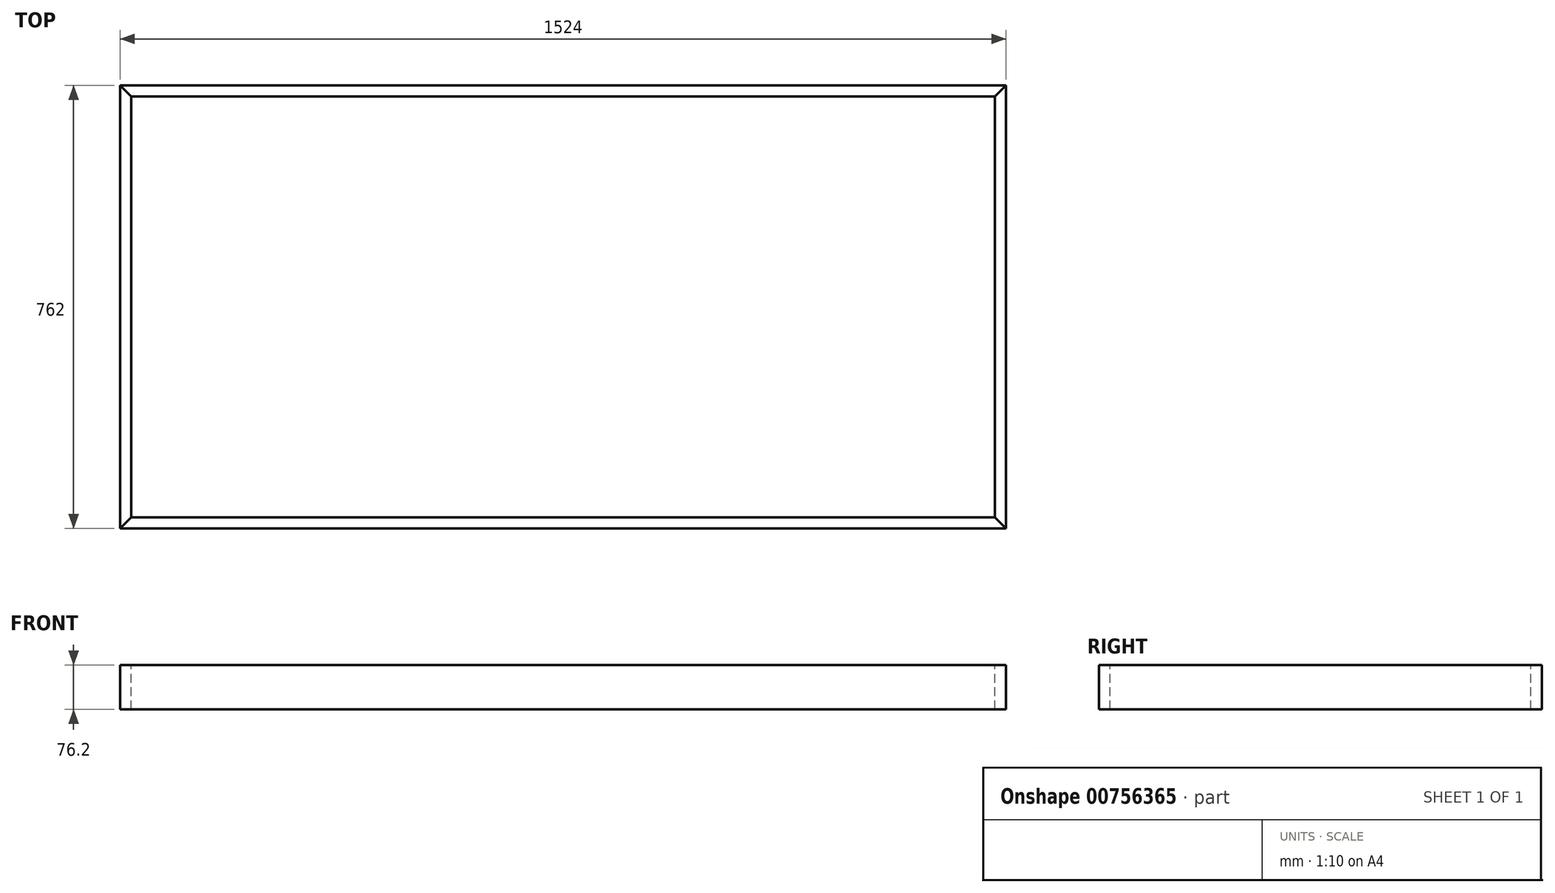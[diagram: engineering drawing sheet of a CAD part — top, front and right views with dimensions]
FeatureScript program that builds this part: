
annotation { "Feature Type Name" : "Feature", "Feature Type Description" : "" }
export const myFeature = defineFeature(function(context is Context, id is Id, definition is map)
    precondition{}
    {
        {
            var Q0;
            Q0=qCreatedBy(makeId("Top.planeOp"),FACE);
            var sketch = newSketch(context, id + "F0", { "sketchPlane" : qUnion([Q0])});
            skLineSegment(sketch, "E0.bottom", {"start": v(762, -381) * mm, "end": v(-762, -381) * mm});
            skLineSegment(sketch, "E0.top", {"start": v(762, 381) * mm, "end": v(-762, 381) * mm});
            skLineSegment(sketch, "E0.left", {"start": v(762, -381) * mm, "end": v(762, 381) * mm});
            skLineSegment(sketch, "E0.right", {"start": v(-762, -381) * mm, "end": v(-762, 381) * mm});
            skPoint(sketch, "E0.middle", {"position": v(0, 0) * mm});
            skSolve(sketch);
        }
        {
            var Q0;
            Q0=qCreatedBy(makeId("Top.planeOp"),FACE);
            var sketch = newSketch(context, id + "F1", { "sketchPlane" : qUnion([Q0])});
            skLineSegment(sketch, "E1.bottom", {"start": v(762, -381) * mm, "end": v(-762, -381) * mm});
            skLineSegment(sketch, "E1.top", {"start": v(762, 381) * mm, "end": v(-762, 381) * mm});
            skLineSegment(sketch, "E1.left", {"start": v(762, -381) * mm, "end": v(762, 381) * mm});
            skLineSegment(sketch, "E1.right", {"start": v(-762, -381) * mm, "end": v(-762, 381) * mm});
            skPoint(sketch, "E1.middle", {"position": v(0, 0) * mm});
            skLineSegment(sketch, "E2.0", {"start": v(742.95, 361.95) * mm, "end": v(-742.95, 361.95) * mm});
            skLineSegment(sketch, "E2.1", {"start": v(742.95, -361.95) * mm, "end": v(742.95, 361.95) * mm});
            skLineSegment(sketch, "E2.2", {"start": v(742.95, -361.95) * mm, "end": v(-742.95, -361.95) * mm});
            skLineSegment(sketch, "E2.3", {"start": v(-742.95, -361.95) * mm, "end": v(-742.95, 361.95) * mm});
            skLineSegment(sketch, "E3", {"start": v(-762, 381) * mm, "end": v(-742.95, 361.95) * mm});
            skLineSegment(sketch, "E4", {"start": v(742.95, 361.95) * mm, "end": v(762, 381) * mm});
            skLineSegment(sketch, "E5", {"start": v(742.95, -361.95) * mm, "end": v(762, -381) * mm});
            skLineSegment(sketch, "E6", {"start": v(-762, -381) * mm, "end": v(-742.95, -361.95) * mm});
            skSolve(sketch);
        }
        {
            var Q0;
            Q0=makeQuery(id+"F1.imprint","IMPRINT",FACE,{"disambiguationData":[TD([[makeQuery(id+"F1.imprint","IMPRINT",EDGE,{"derivedFrom":sQuery(id+"F1.wireOp",EDGE,"E1.right")}),-1.0]])]});
            extrude(context, id + "F2", {"entities" : qUnion([Q0]), "oppositeDirection" : true, "depth" : 76.2 * mm, "offsetDistance" : 25.4 * mm});
        }
        {
            var Q0;
            Q0=makeQuery(id+"F1.imprint","IMPRINT",FACE,{"disambiguationData":[TD([[makeQuery(id+"F1.imprint","IMPRINT",EDGE,{"derivedFrom":sQuery(id+"F1.wireOp",EDGE,"E1.top")}),1.0]])]});
            extrude(context, id + "F3", {"entities" : qUnion([Q0]), "oppositeDirection" : true, "depth" : 76.2 * mm, "offsetDistance" : 25.4 * mm});
        }
        {
            var Q0;
            Q0=makeQuery(id+"F3.opExtrude","SWEPT_BODY",BODY,{"disambiguationData":[OSD([sQuery(id+"F1.wireOp",EDGE,"E1.top"),sQuery(id+"F1.wireOp",EDGE,"E2.0"),sQuery(id+"F1.wireOp",EDGE,"E3"),sQuery(id+"F1.wireOp",EDGE,"E4")])]});
            var Q1;
            Q1=qCreatedBy(makeId("Front.planeOp"),FACE);
            mirror(context, id + "F4", {"entities" : qUnion([Q0]), "mirrorPlane" : qUnion([Q1])});
        }
        {
            var Q0;
            Q0=makeQuery(id+"F2.opExtrude","SWEPT_BODY",BODY,{"disambiguationData":[OSD([sQuery(id+"F1.wireOp",EDGE,"E1.right"),sQuery(id+"F1.wireOp",EDGE,"E2.3"),sQuery(id+"F1.wireOp",EDGE,"E3"),sQuery(id+"F1.wireOp",EDGE,"E6")])]});
            var Q1;
            Q1=qCreatedBy(makeId("Right.planeOp"),FACE);
            mirror(context, id + "F5", {"entities" : qUnion([Q0]), "mirrorPlane" : qUnion([Q1])});
        }
    });
